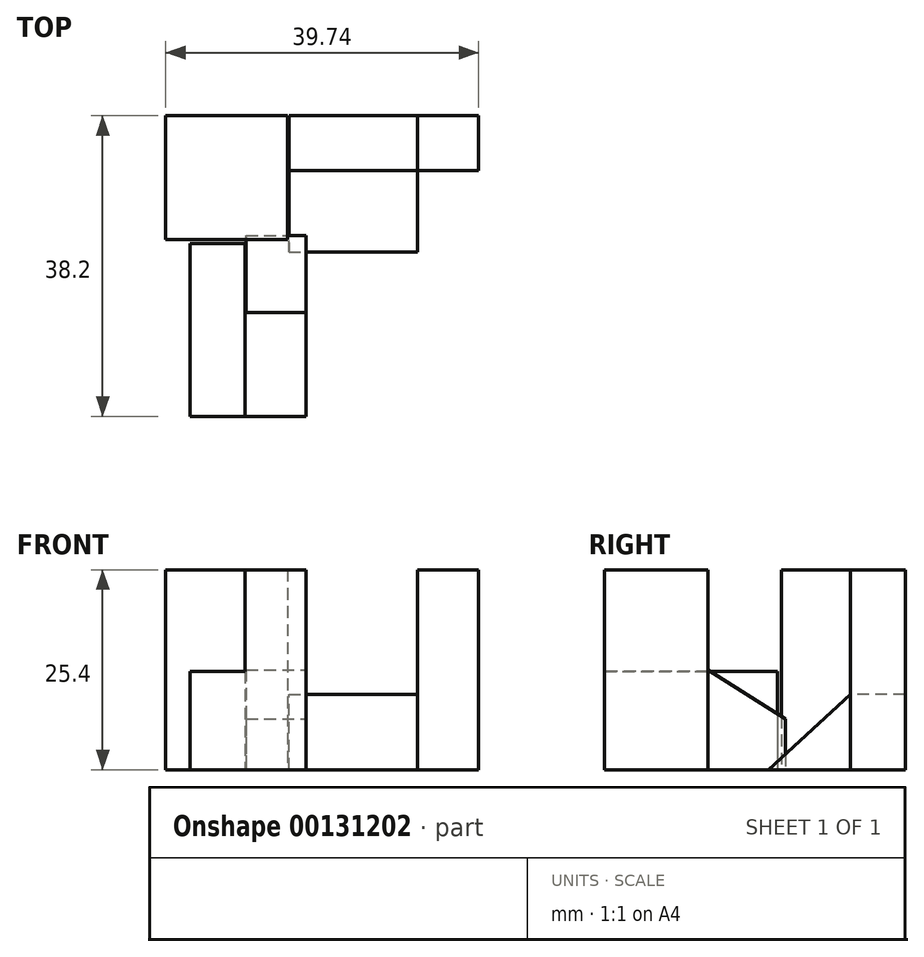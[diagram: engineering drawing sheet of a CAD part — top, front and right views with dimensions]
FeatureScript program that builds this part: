
annotation { "Feature Type Name" : "Feature", "Feature Type Description" : "" }
export const myFeature = defineFeature(function(context is Context, id is Id, definition is map)
    precondition{}
    {
        {
            var Q0;
            Q0=qCreatedBy(makeId("Top.planeOp"),FACE);
            var sketch = newSketch(context, id + "F0", { "sketchPlane" : qUnion([Q0])});
            skLineSegment(sketch, "E0", {"start": v(-60.65, 55.5) * mm, "end": v(-60.65, 39.75) * mm});
            skLineSegment(sketch, "E1", {"start": v(-60.65, 39.75) * mm, "end": v(-45.17, 39.75) * mm});
            skLineSegment(sketch, "E2", {"start": v(-45.17, 39.75) * mm, "end": v(-45.17, 55.5) * mm});
            skLineSegment(sketch, "E3", {"start": v(-45.17, 55.5) * mm, "end": v(-60.65, 55.5) * mm});
            skSolve(sketch);
        }
        {
            var Q0;
            Q0=qCreatedBy(makeId("Top.planeOp"),FACE);
            var sketch = newSketch(context, id + "F1", { "sketchPlane" : qUnion([Q0])});
            skLineSegment(sketch, "E4", {"start": v(-50.59, 17.3) * mm, "end": v(-50.59, 30.46) * mm});
            skLineSegment(sketch, "E5", {"start": v(-50.59, 30.46) * mm, "end": v(-42.84, 30.46) * mm});
            skLineSegment(sketch, "E6", {"start": v(-42.84, 30.46) * mm, "end": v(-42.84, 17.3) * mm});
            skLineSegment(sketch, "E7", {"start": v(-42.84, 17.3) * mm, "end": v(-50.59, 17.3) * mm});
            skSolve(sketch);
        }
        {
            var Q0;
            Q0 = qSketchRegion(id + "F0", true);
            extrude(context, id + "F2", {"entities" : qUnion([Q0]), "depth" : 25.4 * mm});
        }
        {
            var Q0;
            Q0 = qSketchRegion(id + "F1", true);
            extrude(context, id + "F3", {"entities" : qUnion([Q0]), "depth" : 25.4 * mm});
        }
        {
            var Q0;
            Q0=qCreatedBy(makeId("Top.planeOp"),FACE);
            var sketch = newSketch(context, id + "F4", { "sketchPlane" : qUnion([Q0])});
            skLineSegment(sketch, "E8", {"start": v(-28.65, 48.52) * mm, "end": v(-20.9, 48.52) * mm});
            skLineSegment(sketch, "E9", {"start": v(-20.9, 48.52) * mm, "end": v(-20.9, 55.5) * mm});
            skLineSegment(sketch, "E10", {"start": v(-20.9, 55.5) * mm, "end": v(-28.65, 55.5) * mm});
            skLineSegment(sketch, "E11", {"start": v(-28.65, 48.52) * mm, "end": v(-28.65, 55.5) * mm});
            skSolve(sketch);
        }
        {
            var Q0;
            Q0 = qSketchRegion(id + "F4", true);
            extrude(context, id + "F5", {"entities" : qUnion([Q0]), "depth" : 25.4 * mm});
        }
        {
            var Q0;
            Q0=qCreatedBy(makeId("Top.planeOp"),FACE);
            var sketch = newSketch(context, id + "F6", { "sketchPlane" : qUnion([Q0])});
            skLineSegment(sketch, "E12", {"start": v(-50.59, 17.3) * mm, "end": v(-57.56, 17.3) * mm});
            skLineSegment(sketch, "E13", {"start": v(-57.56, 17.3) * mm, "end": v(-57.56, 39.23) * mm});
            skLineSegment(sketch, "E14", {"start": v(-57.56, 39.23) * mm, "end": v(-50.59, 39.23) * mm});
            skLineSegment(sketch, "E15", {"start": v(-50.59, 39.23) * mm, "end": v(-50.59, 17.3) * mm});
            skSolve(sketch);
        }
        {
            var Q0;
            Q0 = qSketchRegion(id + "F6", true);
            extrude(context, id + "F7", {"entities" : qUnion([Q0]), "operationType" : NewBodyOperationType.ADD, "depth" : 12.5 * mm});
        }
        {
            var Q0;
            Q0=makeQuery(id+"F3.opExtrude","SWEPT_FACE",FACE,{"disambiguationData":[OSD([sQuery(id+"F1.wireOp",EDGE,"E6")])]});
            var sketch = newSketch(context, id + "F8", { "sketchPlane" : qUnion([Q0])});
            skLineSegment(sketch, "E16", {"start": v(30.46, 12.7) * mm, "end": v(40.26, 6.45) * mm});
            skLineSegment(sketch, "E17", {"start": v(40.26, 6.45) * mm, "end": v(40.26, 0) * mm});
            skLineSegment(sketch, "E18", {"start": v(40.26, 0) * mm, "end": v(30.46, 0) * mm});
            skLineSegment(sketch, "E19", {"start": v(30.46, 0) * mm, "end": v(30.46, 12.7) * mm});
            skSolve(sketch);
        }
        {
            var Q0;
            Q0 = qSketchRegion(id + "F8", true);
            extrude(context, id + "F9", {"entities" : qUnion([Q0]), "oppositeDirection" : true, "depth" : 7.6 * mm});
        }
        {
            var Q0;
            Q0=makeQuery(id+"F5.opExtrude","SWEPT_FACE",FACE,{"disambiguationData":[OSD([sQuery(id+"F4.wireOp",EDGE,"E11")])]});
            var sketch = newSketch(context, id + "F10", { "sketchPlane" : qUnion([Q0])});
            skLineSegment(sketch, "E20", {"start": v(-55.5, 9.55) * mm, "end": v(-48.52, 9.55) * mm});
            skLineSegment(sketch, "E21", {"start": v(-55.5, 2.58) * mm, "end": v(-55.5, 9.55) * mm});
            skLineSegment(sketch, "E22", {"start": v(-55.5, 9.55) * mm, "end": v(-55.5, 0) * mm});
            skLineSegment(sketch, "E23", {"start": v(-55.5, 0) * mm, "end": v(-38.14, 0) * mm});
            skPoint(sketch, "E23.endSnap0", {"position": v(-52, 0) * mm});
            skLineSegment(sketch, "E24", {"start": v(-38.14, 0) * mm, "end": v(-48.52, 9.55) * mm});
            skSolve(sketch);
        }
        {
            var Q0;
            Q0 = qSketchRegion(id + "F10", true);
            extrude(context, id + "F11", {"entities" : qUnion([Q0]), "depth" : 16.37 * mm});
        }
    });
